# Revit family: BoelsRental_ScissorLift_SKYJACK_SJ6832RTa
name_source: partatom
category: Site
units: mm (PartAtom-declared; Revit-internal decimal feet)

## family parameters
Always vertical = Yes
Cut with Voids When Loaded = No
OmniClass Number = 23.50.05.14.11
OmniClass Title = Scissors Lifts
Part Type = Normal
Round Connector Dimension = Use Diameter
Shared = No
Work Plane-Based = No

## types (1)
- SJ6832RT
    Assembly Code = E1030100
    AssetType = Movable
    BIMObjectName = BoelsRental_ScissorLift_SKYJACK_SJ6832RT
    BoelsSubgroup = 18004 - Scissor lift 11.8m
    Capacity = 454 kg
    ClassificationName = Uniclass2015
    ClassificationValue = Pr_65_80_47_95
    Cost = 0 $
    Description = SCISSOR LIFT, SELF PROPELLED, DIESEL < 10 M, WITH OUTRIGGERS
    DocumentationCertificates = https://www.boels.com
    DocumentationInstallationGuide = https://www.boels.com
    DocumentationLiterature = https://www.boels.com
    DocumentationMaintenance = https://www.boels.com
    DocumentationTechnical = https://www.boels.com
    DurationUnit = Years
    ExpectedLife = 0
    ExtensionDeckRollOut = 1.52 m
    Gradeability = 40%
    GroundClearance = 200 mm  [stored 0.656168 ft]
    IfcExportAs = IfcTransportElement
    IfcExportType = IfcTransportElementType
    InsideTurningRadius = 1.52 m
    Keynote = X
    LiftTimeWithRatedLoad = 39 sec
    LocalFloorLoadWithRatedLoad = 1248 kPa
    LowerTimeWithRatedLoad = 36 sec
    LoweredPlatformHeight = 1370 mm
    Manufacturer = Boels Rental (SKYJACK)
    ManufacturerName = Boels Rental (SKYJACK)
    Material = Steel
    MaximumNumberOfPersons = 4/4 (to 7.92m) 2 (to 9.75m)
    Model = Scissor Lift - SJ6832RT
    ModelNumber = SJ6832RT
    ModelReference = Scissor Lift
    NBSDescription = Vertical lifting platforms
    NBSObjectName = Boels Rental - Vertical lifting platforms
    NBSReference = 90-80-65/350
    NominalDepth = 0 mm  [stored 0 ft]
    NominalHeight = 0 mm  [stored 0 ft]
    NominalLength = 0 mm  [stored 0 ft]
    OutsideTurningRadius = 3.96 m
    OverallFloorLoadWithRatedLoad = 14 kPa
    OverallHeight = 2510 mm
    OverallLength = 3350 mm
    OverallWidth = 1760 mm
    ProductPageLink = https://www.boels.com
    ProductionYear = 2022
    RaisedDriveSpeed = 0.6 km/h
    RaisedPlatformHeight = 9750 mm
    StowedDriveSpeed = 6.1 km/h
    TireSize = 26 x 12
    TireType = Foam Filled
    Type Comments = Scissor Lift - SJ6832RT
    TypeName = Scissor Lift - SJ6832RT
    URL = https://www.boels.com
    WarrantyDurationLabor = 0
    WarrantyDurationParts = 0
    WarrantyDurationUnit = Years
    WarrantyGuarantorLabor = https://www.boels.com
    WarrantyGuarantorParts = https://www.boels.com
    Weight = 3,781 kg
    Wheelbase = 2040 mm
    WorkingHeight = 11750 mm
    _BSBibleVersion = 16
    _BimSpecGuid = 0
    _CurrentRevision = 1
    _DistributedBy = https://www.boels.com
    _ObjectUserGuide = https://www.boels.com

note: [stored X ft] marks values corroborated as IEEE doubles in the binary element streams (Revit-internal decimal feet)

## geometry (parser evidence)
native form markers: Sweep x33
no freeform markers — native parametric forms only
